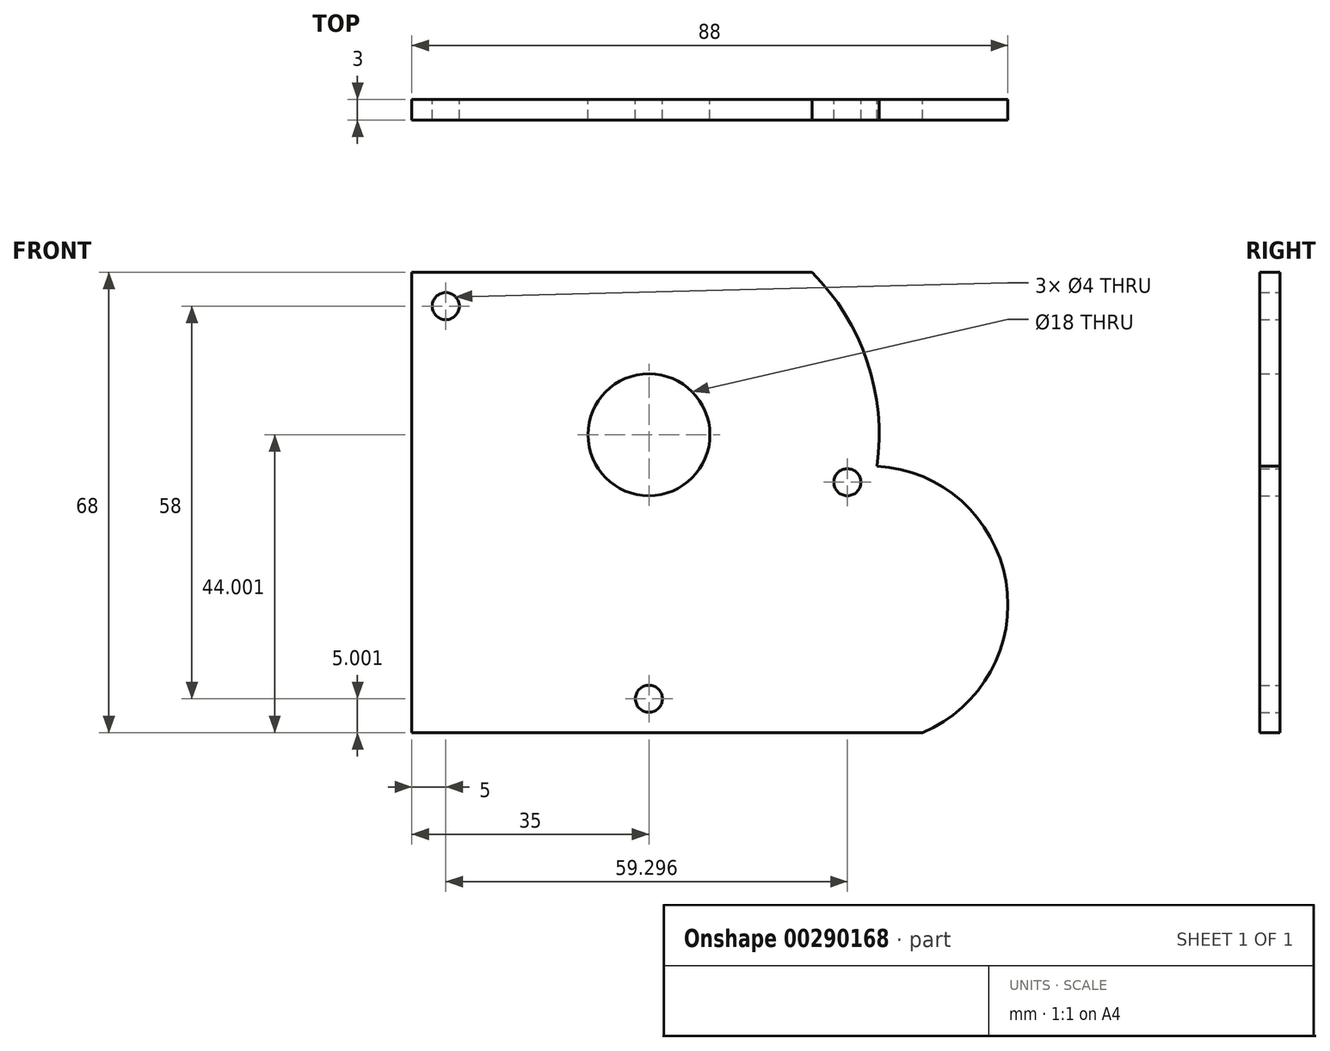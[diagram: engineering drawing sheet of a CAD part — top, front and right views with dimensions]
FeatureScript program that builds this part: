
annotation { "Feature Type Name" : "Feature", "Feature Type Description" : "" }
export const myFeature = defineFeature(function(context is Context, id is Id, definition is map)
    precondition{}
    {
        {
            var Q0;
            Q0=qCreatedBy(makeId("Front.planeOp"),FACE);
            var sketch = newSketch(context, id + "F0", { "sketchPlane" : qUnion([Q0])});
            skLineSegment(sketch, "E0.bottom", {"start": v(-35, 36.6) * mm, "end": v(24.08, 36.6) * mm});
            skLineSegment(sketch, "E0.top", {"start": v(-35, -31.4) * mm, "end": v(40.4, -31.4) * mm});
            skLineSegment(sketch, "E0.left", {"start": v(-35, 36.6) * mm, "end": v(-35, -31.4) * mm});
            skCircle(sketch, "E1", {"center": v(0, 12.6) * mm, "radius": 9 * mm});
            skArc(sketch, "E2", {"start": v(33.68, 7.98) * mm, "mid": v(32.23, 23.42) * mm, "end": v(24.08, 36.6) * mm});
            skArc(sketch, "E3", {"start": v(40.4, -31.4) * mm, "mid": v(52.7, -9.04) * mm, "end": v(33.68, 7.98) * mm});
            skCircle(sketch, "E4", {"center": v(-30, 31.6) * mm, "radius": 2 * mm});
            skCircle(sketch, "E5", {"center": v(29.3, 5.59) * mm, "radius": 2 * mm});
            skCircle(sketch, "E6", {"center": v(0, -26.4) * mm, "radius": 2 * mm});
            skSolve(sketch);
        }
        {
            var Q0;
            Q0=makeQuery(id+"F0.imprint","IMPRINT",FACE,{"disambiguationData":[TD([[makeQuery(id+"F0.imprint","IMPRINT",EDGE,{"derivedFrom":sQuery(id+"F0.wireOp",EDGE,"E0.bottom")}),-1.0]])]});
            extrude(context, id + "F1", {"entities" : qUnion([Q0]), "depth" : 3 * mm});
        }
    });
